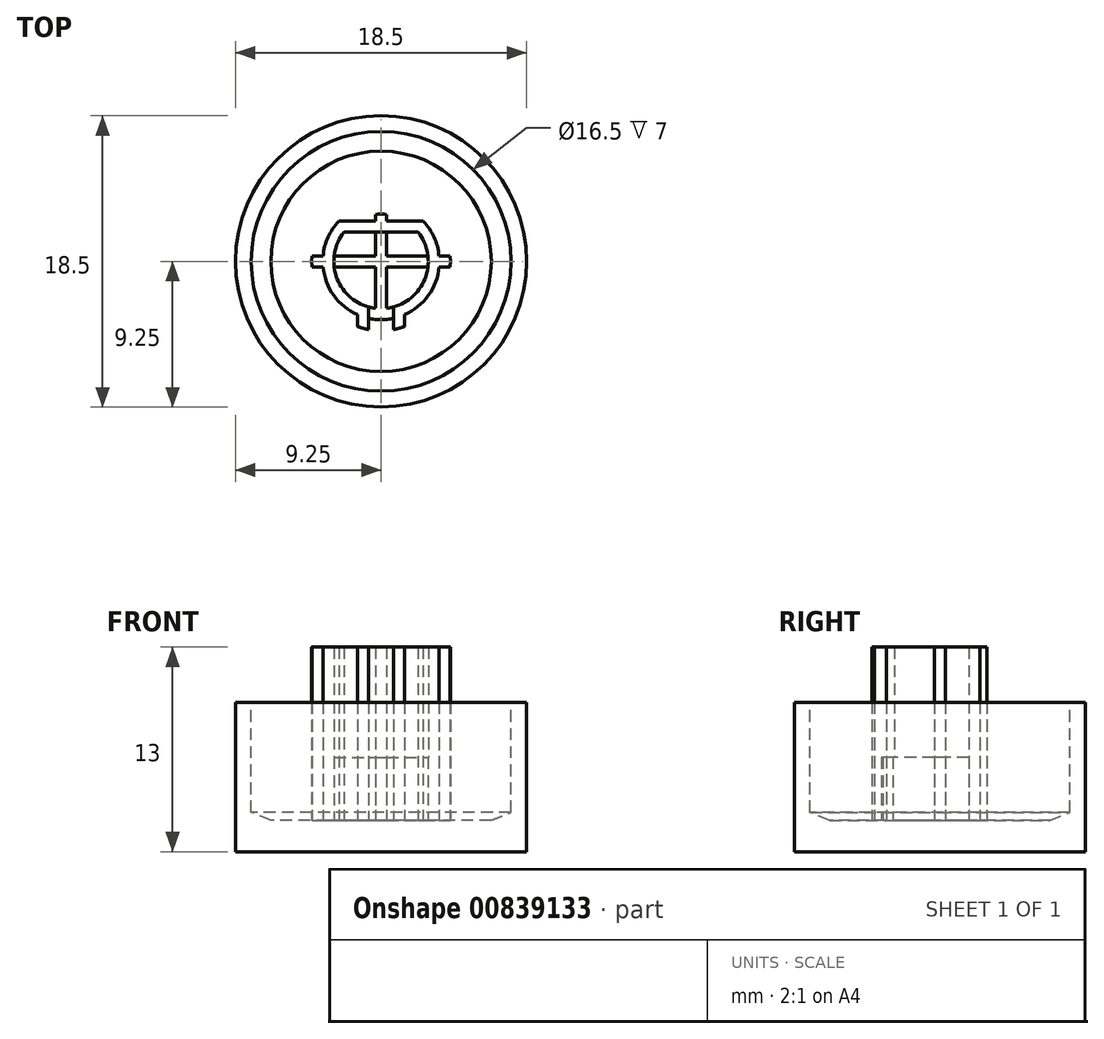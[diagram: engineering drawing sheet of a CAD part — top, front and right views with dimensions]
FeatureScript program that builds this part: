
annotation { "Feature Type Name" : "Feature", "Feature Type Description" : "" }
export const myFeature = defineFeature(function(context is Context, id is Id, definition is map)
    precondition{}
    {
        {
            var Q0;
            Q0=qCreatedBy(makeId("Front.planeOp"),FACE);
            var sketch = newSketch(context, id + "F0", { "sketchPlane" : qUnion([Q0])});
            skLineSegment(sketch, "E0", {"start": v(0, 7.05) * mm, "end": v(0, -7.62) * mm, "construction": true});
            skLineSegment(sketch, "E1", {"start": v(0, 0) * mm, "end": v(9.25, 0) * mm});
            skLineSegment(sketch, "E2", {"start": v(9.25, 0) * mm, "end": v(9.25, 9.5) * mm});
            skLineSegment(sketch, "E3", {"start": v(8.25, 9.5) * mm, "end": v(8.25, 2.5) * mm});
            skLineSegment(sketch, "E4", {"start": v(7, 2) * mm, "end": v(0, 2) * mm});
            skLineSegment(sketch, "E5", {"start": v(8.25, 9.5) * mm, "end": v(9.25, 9.5) * mm});
            skLineSegment(sketch, "E6", {"start": v(0, 2) * mm, "end": v(0, 0) * mm});
            skLineSegment(sketch, "E7.trimOffspring", {"start": v(8.25, 2.5) * mm, "end": v(7, 2) * mm});
            skSolve(sketch);
        }
        {
            var Q0;
            Q0=qSketchRegion(id+"F0",true);
            var Q1;
            Q1=sQuery(id+"F0.wireOp",EDGE,"E0");
            revolve(context, id + "F1", {"surfaceOperationType" : NewSurfaceOperationType.NEW, "entities" : qUnion([Q0]), "axis" : qUnion([Q1]), "revolveType" : RevolveType.FULL});
        }
        {
            var Q0;
            Q0=qCreatedBy(makeId("Top.planeOp"),FACE);
            var sketch = newSketch(context, id + "F2", { "sketchPlane" : qUnion([Q0])});
            skArc(sketch, "E8", {"start": v(0.35, 2.98) * mm, "mid": v(0, 3) * mm, "end": v(-0.35, 2.98) * mm});
            skArc(sketch, "E9", {"start": v(-2.68, 2.55) * mm, "mid": v(-3.63, -0.73) * mm, "end": v(-1.49, -3.39) * mm});
            skLineSegment(sketch, "E10", {"start": v(-2.68, 2.55) * mm, "end": v(2.68, 2.55) * mm});
            skLineSegment(sketch, "E11", {"start": v(-2.36, 1.85) * mm, "end": v(2.36, 1.85) * mm});
            skLineSegment(sketch, "E12", {"start": v(-4.39, 0.35) * mm, "end": v(-0.35, 0.35) * mm});
            skLineSegment(sketch, "E13", {"start": v(-4.39, -0.35) * mm, "end": v(-0.35, -0.35) * mm});
            skLineSegment(sketch, "E14", {"start": v(-0.35, 2.98) * mm, "end": v(-0.35, 0.35) * mm});
            skLineSegment(sketch, "E15", {"start": v(0.35, 2.98) * mm, "end": v(0.35, 0.35) * mm});
            skLineSegment(sketch, "E16", {"start": v(-0.79, -2.9) * mm, "end": v(-0.79, -4.33) * mm});
            skLineSegment(sketch, "E17", {"start": v(0.79, -2.9) * mm, "end": v(0.79, -4.33) * mm});
            skLineSegment(sketch, "E18", {"start": v(0, 3.7) * mm, "end": v(0, -3.7) * mm, "construction": true});
            skLineSegment(sketch, "E19", {"start": v(3.7, 0) * mm, "end": v(-3.7, 0) * mm, "construction": true});
            skArc(sketch, "E20", {"start": v(-4.39, 0.35) * mm, "mid": v(-4.4, 0) * mm, "end": v(-4.39, -0.35) * mm});
            skLineSegment(sketch, "E21", {"start": v(-1.49, -3.39) * mm, "end": v(-1.49, -4.14) * mm});
            skLineSegment(sketch, "E22", {"start": v(1.49, -3.39) * mm, "end": v(1.49, -4.14) * mm});
            skArc(sketch, "E23.trimOffspring", {"start": v(-1.49, -4.14) * mm, "mid": v(-1.14, -4.25) * mm, "end": v(-0.79, -4.33) * mm});
            skArc(sketch, "E24.trimOffspring", {"start": v(0.79, -4.33) * mm, "mid": v(1.14, -4.25) * mm, "end": v(1.49, -4.14) * mm});
            skArc(sketch, "E25.trimOffspring", {"start": v(4.39, -0.35) * mm, "mid": v(4.4, 0) * mm, "end": v(4.39, 0.35) * mm});
            skArc(sketch, "E26.trimOffspring", {"start": v(-2.36, 1.85) * mm, "mid": v(-2.77, -1.15) * mm, "end": v(-0.35, -2.98) * mm});
            skArc(sketch, "E27.trimOffspring", {"start": v(-0.79, -3.62) * mm, "mid": v(0, -3.7) * mm, "end": v(0.79, -3.62) * mm});
            skArc(sketch, "E28.trimOffspring", {"start": v(1.49, -3.39) * mm, "mid": v(3.63, -0.73) * mm, "end": v(2.68, 2.55) * mm});
            skArc(sketch, "E29.trimOffspring", {"start": v(0.35, -2.98) * mm, "mid": v(2.77, -1.15) * mm, "end": v(2.36, 1.85) * mm});
            skLineSegment(sketch, "E30.trimOffspring", {"start": v(0.35, -0.35) * mm, "end": v(0.35, -2.98) * mm});
            skLineSegment(sketch, "E31.trimOffspring", {"start": v(-0.35, -0.35) * mm, "end": v(-0.35, -2.98) * mm});
            skLineSegment(sketch, "E32.trimOffspring", {"start": v(0.35, 0.35) * mm, "end": v(4.39, 0.35) * mm});
            skLineSegment(sketch, "E33.trimOffspring", {"start": v(0.35, -0.35) * mm, "end": v(4.39, -0.35) * mm});
            skSolve(sketch);
        }
        {
            var Q0;
            {var subQ8=sQuery(id+"F2.wireOp",EDGE,"E21");Q0=makeQuery(id+"F2.imprint","IMPRINT",FACE,{"disambiguationData":[TD([[makeQuery(id+"F2.imprint","IMPRINT",EDGE,{"derivedFrom":subQ8}),1.0]])]});}
            var Q1;
            {var subQ5=sQuery(id+"F2.wireOp",EDGE,"E10");var subQ6=sQuery(id+"F2.wireOp",EDGE,"E9");var subQ7=makeQuery(id+"F2.imprint","INTERSECT",VERTEX,{"derivedFrom":[subQ6,subQ5]});Q1=makeQuery(id+"F2.imprint","IMPRINT",FACE,{"disambiguationData":[TD([[makeQuery(id+"F2.imprint","IMPRINT",EDGE,{"disambiguationData":[TD([[subQ7,-1.0]])],"derivedFrom":subQ6}),1.0]])]});}
            var Q2;
            {var subQ1=sQuery(id+"F2.wireOp",EDGE,"E10");var subQ7=sQuery(id+"F2.wireOp",EDGE,"E28.trimOffspring");var subQ8=makeQuery(id+"F2.imprint","INTERSECT",VERTEX,{"derivedFrom":[subQ1,subQ7]});Q2=makeQuery(id+"F2.imprint","IMPRINT",FACE,{"disambiguationData":[TD([[makeQuery(id+"F2.imprint","IMPRINT",EDGE,{"disambiguationData":[TD([[subQ8,1.0]])],"derivedFrom":subQ1}),-1.0]])]});}
            var Q3;
            {var subQ0=sQuery(id+"F2.wireOp",EDGE,"E33.trimOffspring");var subQ1=sQuery(id+"F2.wireOp",EDGE,"E28.trimOffspring");var subQ2=makeQuery(id+"F2.imprint","INTERSECT",VERTEX,{"derivedFrom":[subQ1,subQ0]});Q3=makeQuery(id+"F2.imprint","IMPRINT",FACE,{"disambiguationData":[TD([[makeQuery(id+"F2.imprint","IMPRINT",EDGE,{"disambiguationData":[TD([[subQ2,-1.0]])],"derivedFrom":subQ1}),1.0]])]});}
            var Q4;
            {var subQ0=sQuery(id+"F2.wireOp",EDGE,"E14");var subQ1=sQuery(id+"F2.wireOp",EDGE,"E10");var subQ2=makeQuery(id+"F2.imprint","INTERSECT",VERTEX,{"derivedFrom":[subQ1,subQ0]});Q4=makeQuery(id+"F2.imprint","IMPRINT",FACE,{"disambiguationData":[TD([[makeQuery(id+"F2.imprint","IMPRINT",EDGE,{"disambiguationData":[TD([[subQ2,-1.0]])],"derivedFrom":subQ1}),-1.0]])]});}
            var Q5;
            {var subQ0=sQuery(id+"F2.wireOp",EDGE,"E12");var subQ1=sQuery(id+"F2.wireOp",EDGE,"E9");var subQ2=makeQuery(id+"F2.imprint","INTERSECT",VERTEX,{"derivedFrom":[subQ1,subQ0]});Q5=makeQuery(id+"F2.imprint","IMPRINT",FACE,{"disambiguationData":[TD([[makeQuery(id+"F2.imprint","IMPRINT",EDGE,{"disambiguationData":[TD([[subQ2,-1.0]])],"derivedFrom":subQ1}),1.0]])]});}
            var Q6;
            {var subQ0=sQuery(id+"F2.wireOp",EDGE,"E22");Q6=makeQuery(id+"F2.imprint","IMPRINT",FACE,{"disambiguationData":[TD([[makeQuery(id+"F2.imprint","IMPRINT",EDGE,{"derivedFrom":subQ0}),-1.0]])]});}
            var Q7;
            {var subQ5=sQuery(id+"F2.wireOp",EDGE,"E20");Q7=makeQuery(id+"F2.imprint","IMPRINT",FACE,{"disambiguationData":[TD([[makeQuery(id+"F2.imprint","IMPRINT",EDGE,{"derivedFrom":subQ5}),1.0]])]});}
            var Q8;
            {var subQ0=sQuery(id+"F2.wireOp",EDGE,"E8");Q8=makeQuery(id+"F2.imprint","IMPRINT",FACE,{"disambiguationData":[TD([[makeQuery(id+"F2.imprint","IMPRINT",EDGE,{"derivedFrom":subQ0}),1.0]])]});}
            var Q9;
            {var subQ0=sQuery(id+"F2.wireOp",EDGE,"E25.trimOffspring");Q9=makeQuery(id+"F2.imprint","IMPRINT",FACE,{"disambiguationData":[TD([[makeQuery(id+"F2.imprint","IMPRINT",EDGE,{"derivedFrom":subQ0}),1.0]])]});}
            extrude(context, id + "F3", {"entities" : qUnion([Q0, Q1, Q2, Q3, Q4, Q5, Q6, Q7, Q8, Q9]), "operationType" : NewBodyOperationType.ADD, "depth" : 13 * mm, "offsetDistance" : 25 * mm});
        }
        {
            var Q0;
            {var subQ0=sQuery(id+"F2.wireOp",EDGE,"E27.trimOffspring");Q0=makeQuery(id+"F2.imprint","IMPRINT",FACE,{"disambiguationData":[TD([[makeQuery(id+"F2.imprint","IMPRINT",EDGE,{"derivedFrom":subQ0}),1.0]])]});}
            extrude(context, id + "F4", {"entities" : qUnion([Q0]), "operationType" : NewBodyOperationType.ADD, "depth" : 6 * mm, "offsetDistance" : 25 * mm});
        }
    });
